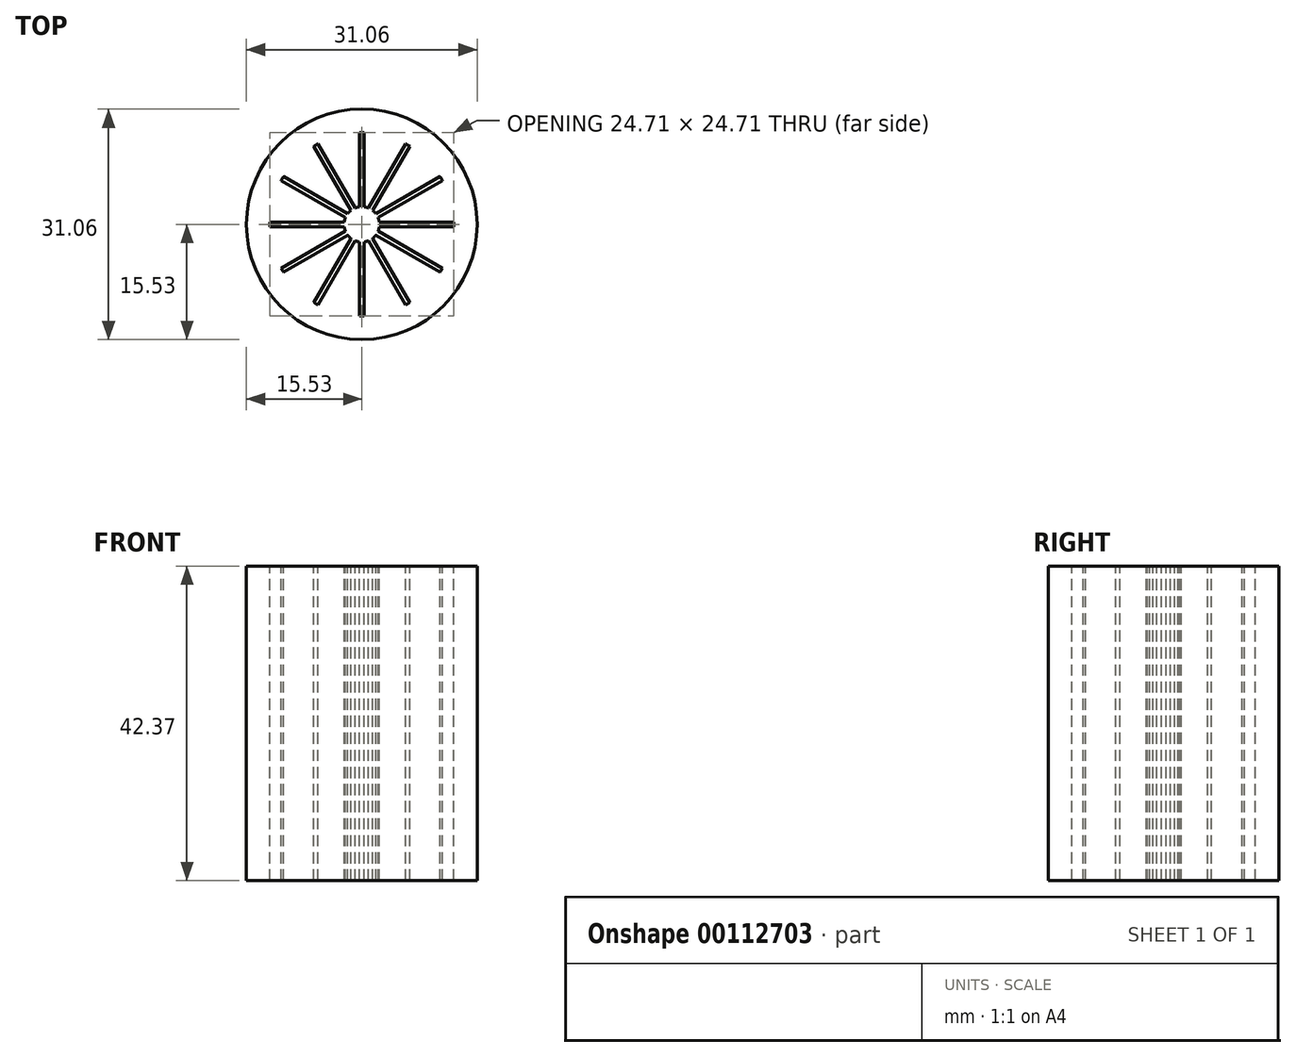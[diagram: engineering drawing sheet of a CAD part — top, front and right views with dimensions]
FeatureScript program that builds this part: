
annotation { "Feature Type Name" : "Feature", "Feature Type Description" : "" }
export const myFeature = defineFeature(function(context is Context, id is Id, definition is map)
    precondition{}
    {
        {
            var Q0;
            Q0=qCreatedBy(makeId("Top.planeOp"),FACE);
            var sketch = newSketch(context, id + "F0", { "sketchPlane" : qUnion([Q0])});
            skCircle(sketch, "E0", {"center": v(0, 0) * mm, "radius": 15.53 * mm});
            skCircle(sketch, "E1", {"center": v(0, 0) * mm, "radius": 2.38 * mm});
            skSolve(sketch);
        }
        {
            var Q0;
            Q0 = qSketchRegion(id + "F0", true);
            extrude(context, id + "F1", {"entities" : qUnion([Q0]), "depth" : 42.37 * mm});
        }
        {
            var Q0;
            Q0=makeQuery(id+"F1.opExtrude","CAP_FACE",FACE,{"disambiguationData":[OSD([sQuery(id+"F0.wireOp",EDGE,"E0"),sQuery(id+"F0.wireOp",EDGE,"E1")])],"isStart":false});
            var sketch = newSketch(context, id + "F2", { "sketchPlane" : qUnion([Q0])});
            skLineSegment(sketch, "E2", {"start": v(0, 0) * mm, "end": v(0, 2.36) * mm});
            skLineSegment(sketch, "E3.bottom", {"start": v(-0.31, 2.36) * mm, "end": v(0.31, 2.36) * mm});
            skLineSegment(sketch, "E3.left", {"start": v(-0.31, 2.36) * mm, "end": v(-0.31, 12.35) * mm});
            skLineSegment(sketch, "E3.right", {"start": v(0.31, 2.36) * mm, "end": v(0.31, 12.35) * mm});
            skLineSegment(sketch, "E4", {"start": v(0.31, 2.36) * mm, "end": v(0, 0) * mm, "construction": true});
            skLineSegment(sketch, "E5", {"start": v(0, 0) * mm, "end": v(-0.31, 2.36) * mm, "construction": true});
            skArc(sketch, "E6", {"start": v(0.31, 12.35) * mm, "mid": v(0, 12.36) * mm, "end": v(-0.31, 12.35) * mm});
            skSolve(sketch);
        }
        {
            var Q0;
            Q0 = qSketchRegion(id + "F2", true);
            var Q1;
            Q1=makeQuery(id+"F1.opExtrude","CAP_FACE",FACE,{"disambiguationData":[OSD([sQuery(id+"F0.wireOp",EDGE,"E0"),sQuery(id+"F0.wireOp",EDGE,"E1")])],"isStart":true});
            extrude(context, id + "F3", {"entities" : qUnion([Q0]), "operationType" : NewBodyOperationType.REMOVE, "endBound" : BoundingType.UP_TO_SURFACE, "oppositeDirection" : true, "endBoundEntityFace" : qUnion([Q1]), "depth" : 25.4 * mm});
        }
        {
            var Q0;
            Q0=makeQuery(id+"F3.boolean.opBoolean","COPY",FACE,{"derivedFrom":makeQuery(id+"F3.opExtrude","SWEPT_FACE",FACE,{"disambiguationData":[OSD([sQuery(id+"F2.wireOp",EDGE,"E3.right")])]})});
            var Q1;
            Q1=makeQuery(id+"F3.boolean.opBoolean","COPY",FACE,{"derivedFrom":makeQuery(id+"F3.opExtrude","SWEPT_FACE",FACE,{"disambiguationData":[OSD([sQuery(id+"F2.wireOp",EDGE,"E6")])]})});
            var Q2;
            Q2=makeQuery(id+"F3.boolean.opBoolean","COPY",FACE,{"derivedFrom":makeQuery(id+"F3.opExtrude","SWEPT_FACE",FACE,{"disambiguationData":[OSD([sQuery(id+"F2.wireOp",EDGE,"E3.left")])]})});
            var Q3;
            Q3=makeQuery(id+"F1.opExtrude","SWEPT_FACE",FACE,{"disambiguationData":[OSD([sQuery(id+"F0.wireOp",EDGE,"E1")])]});
            circularPattern(context, id + "F4", {"patternType" : PatternType.FACE, "faces" : qUnion([Q0, Q1, Q2]), "axis" : qUnion([Q3]), "angle" : 30 * degree, "instanceCount" : 12, "oppositeDirection" : true});
        }
    });
